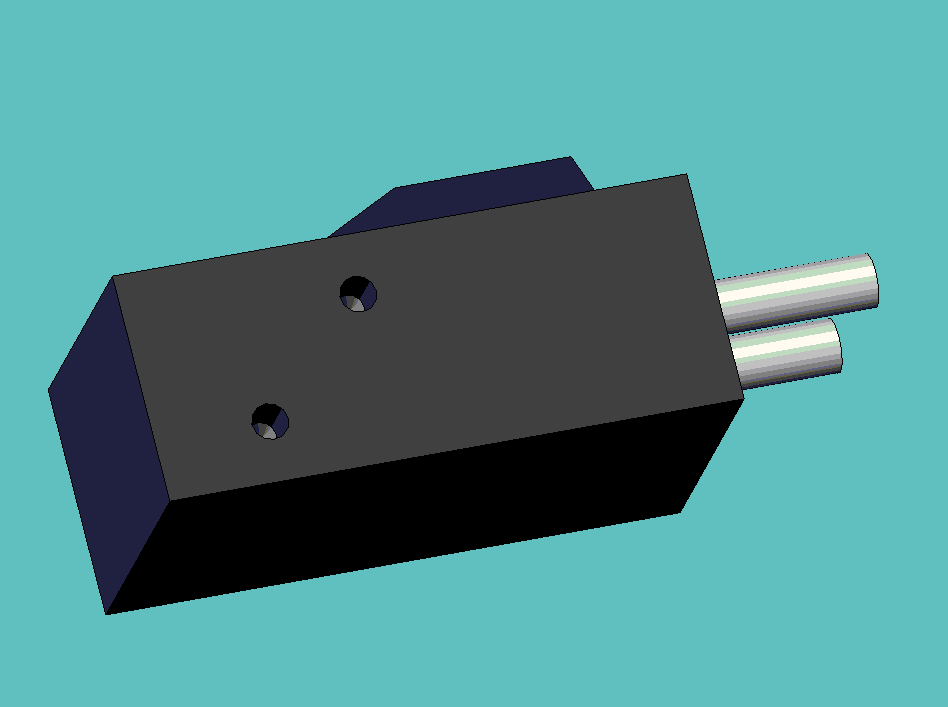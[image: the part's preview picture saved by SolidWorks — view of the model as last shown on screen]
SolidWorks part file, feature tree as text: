
SOLIDWORKS PART (.sldprt)
format: sldprt  version: not decoded by parser v0  size: 253,440 bytes
history: native  units: mm
features: sketch x7, extrude x3, chamfer x3, hole x2, material x1 (+13 scaffold rows collapsed)
feature tree (29):
  scaffold x13  (default folders/planes/origin — collapsed)
  material  "Material <not specified>"
  sketch  "Sketch1"  dims[D1=63.246mm D2=36.83mm]
  extrude  "Extrude1"  Depth=25.4mm
  hole  "M4x0.7 Tapped Hole1"  Diameter=3.3mm Depth=5.08mm
  sketch  "Sketch3"  dims[D1=12.7mm D2=25.4mm D3=6.6675mm D4=12.065mm]
  sketch  "Sketch2"  dims[hole-wizard template sketch: 28 standard entries collapsed; hole parameters kept: c8.Tap Drill Dia.=3.3mm c8.Tap Drill Depth=5.08mm c8.Thread Major Dia.=4.0mm c8.Thread Depth=~8.000009mm c8.D5=~14.816244mm c8.Drill Angle=118.0deg]
  hole  "M4x0.7 Tapped Hole2"  Diameter=3.3mm Depth=5.08mm
  sketch  "Sketch4"  dims[c1.D1=12.7mm c1.D2=25.4mm c1.D3=6.6675mm c1.D4=12.065mm c2.D1=6.6675mm c2.D2=6.6675mm c2.D3=12.7mm c2.D5=25.4mm]
  sketch  "Sketch5"  dims[hole-wizard template sketch: 28 standard entries collapsed; hole parameters kept: c8.Tap Drill Dia.=3.3mm c8.Tap Drill Depth=5.08mm c8.Thread Major Dia.=4.0mm c8.Thread Depth=~8.000009mm c8.D5=~14.816244mm c8.Drill Angle=118.0deg]
  sketch  "Sketch6"  dims[D1=10.16mm D2=23.622mm]
  extrude  "Extrude2"  Depth=5.842mm
  chamfer  "Chamfer1"  Distance=5.842mm Angle=45deg
  chamfer  "Chamfer2"  Distance=5.842mm Angle=45deg
  chamfer  "Chamfer3"  Distance=5.842mm
  sketch  "Sketch7"  dims[c1.D3=5.9563mm c1.D4=5.9563mm c1.D1=10.541mm c1.D2=90.0deg c2.D2=10.541mm]
  extrude  "Extrude3"  Depth=18.5801mm
decode coverage: 15 of 15 modeling features carry decoded parameters
note: ~ marks probable driven/reference dimensions
note: suppression state not decoded; provenance and decode notes live in map.json
